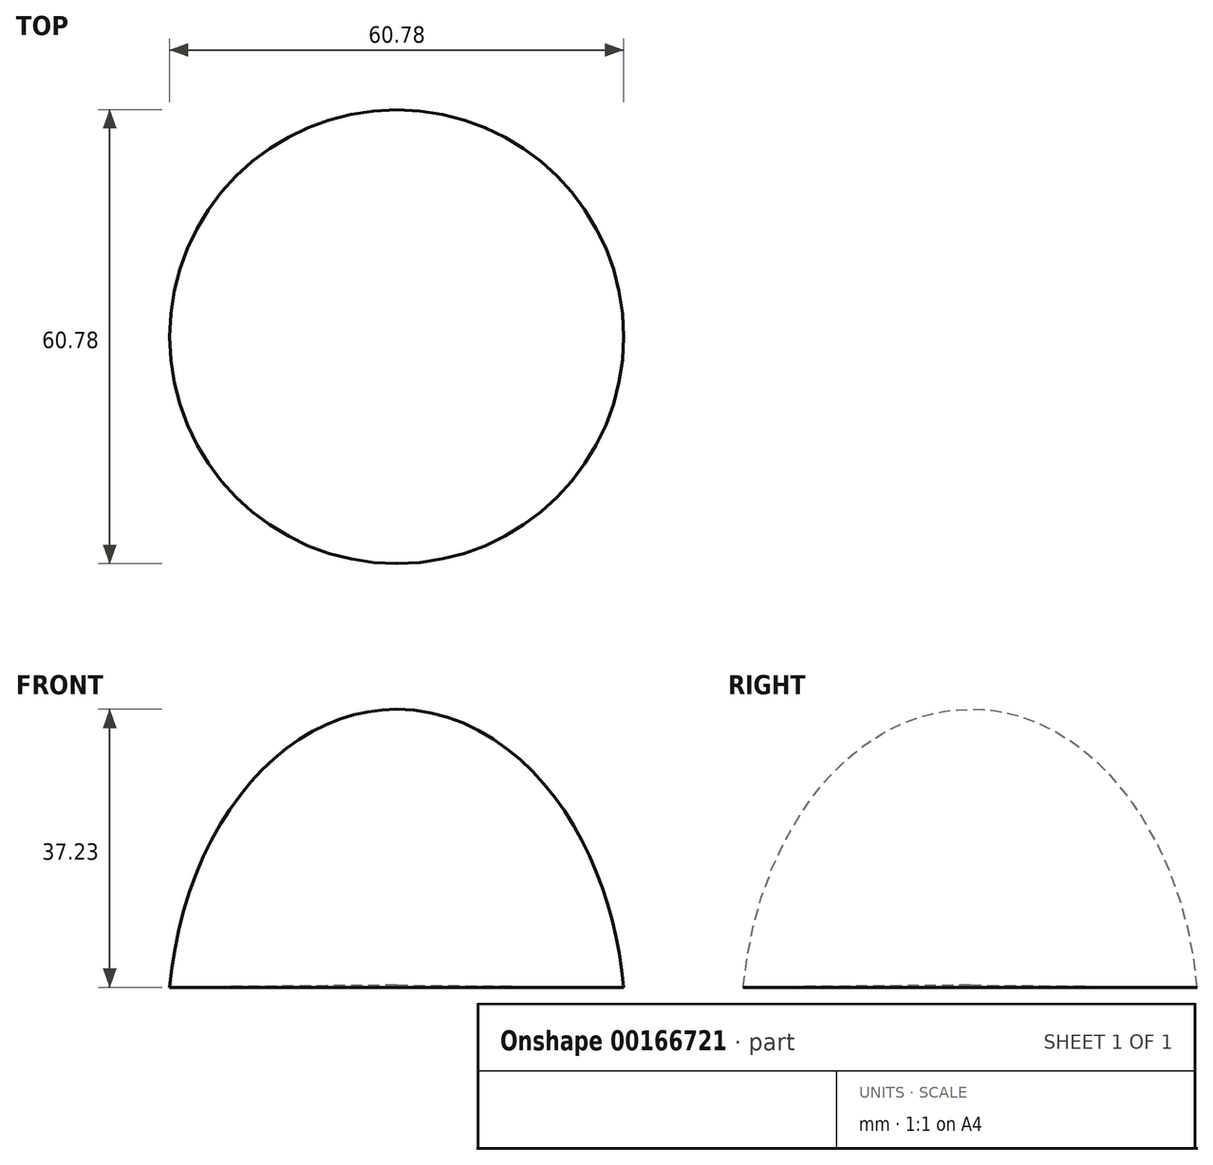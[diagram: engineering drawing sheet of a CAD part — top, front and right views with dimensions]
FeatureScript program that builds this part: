
annotation { "Feature Type Name" : "Feature", "Feature Type Description" : "" }
export const myFeature = defineFeature(function(context is Context, id is Id, definition is map)
    precondition{}
    {
        {
            var Q0;
            Q0=qCreatedBy(makeId("Front.planeOp"),FACE);
            var sketch = newSketch(context, id + "F0", { "sketchPlane" : qUnion([Q0])});
            skEllipticalArc(sketch, "E0", {});
            skLineSegment(sketch, "E1", {"start": v(0, 24.35) * mm, "end": v(0, -60.8) * mm});
            skLineSegment(sketch, "E2", {"start": v(-30.39, -12.88) * mm, "end": v(30.33, -12.31) * mm});
            const initialGuessF0  = {"E0": [0, -0.018226360569867078, 0, 1, 0.04257367890623468, 0.0306303290895846, 4.851738173355985, 1.4448323527280982]};
            skSetInitialGuess(sketch, initialGuessF0);
            skSolve(sketch);
        }
        {
            var Q0;
            {var subQ0=sQuery(id+"F0.wireOp",EDGE,"E1");var subQ1=sQuery(id+"F0.wireOp",EDGE,"E0");var subQ2=makeQuery(id+"F0.imprint","INTERSECT",VERTEX,{"derivedFrom":[subQ1,subQ0]});Q0=makeQuery(id+"F0.imprint","IMPRINT",FACE,{"disambiguationData":[TD([[makeQuery(id+"F0.imprint","IMPRINT",EDGE,{"disambiguationData":[TD([[subQ2,-1.0]])],"derivedFrom":subQ1}),1.0]])]});}
            var Q1;
            Q1=sQuery(id+"F0.wireOp",EDGE,"E1");
            revolve(context, id + "F1", {"entities" : qUnion([Q0]), "axis" : qUnion([Q1]), "revolveType" : RevolveType.FULL});
        }
    });
